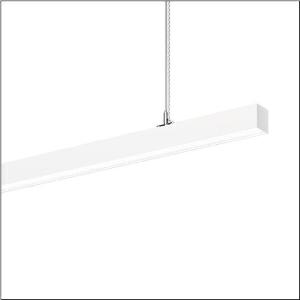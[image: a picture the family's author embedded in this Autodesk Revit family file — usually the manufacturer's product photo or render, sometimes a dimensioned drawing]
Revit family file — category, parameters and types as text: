
# Revit family: silica_21_51mx33dc4dwb
name_source: partatom
category: Lighting Fixtures
units: mm (PartAtom-declared; Revit-internal decimal feet)

## family parameters
Cut with Voids When Loaded = No
Host = Face
Light Source = No
Part Type = Normal
Room Calculation Point = No
Round Connector Dimension = Use Diameter
Shared = No

## types (1)
- --- (1 x LED, 14790 lm, 93.9 W, 4000K)
    Apparent Load = 94 VA
    CIE Flux Codes = 78 96 99 55 100
    Color Rendering = 80
    Color Temperature = 4000K
    Default Elevation = 1800 mm
    Description = Silica 21, office luminaire, primary optical cover: prismatic diffuser, of PMMA, CAT 2 (L<= 3000cd/m²), light emission: direct/indirect distribution, primary light characteristic: symmetric, installation type: suspended mounting, LED, rated luminous flux: 14.790lm, luminous efficacy: 158lm/W, light colour: 840, colour temperature: 4000K, control gear: DALI 2, with terminal, 3+2-pole, max. 2.5mm², mains connection: 220..240V, AC, 50/60Hz, rated input power: 93.9W, luminaire housing, of aluminium, traffic white (RAL 9016), length: 3.004mm, width: 53mm, height: 53mm, protection rating (complete): IP20, insulation class (complete): insulation class I (protective earthing), certification: CE, permissible operating ambient temperature: 0..+35°C, standard: EN 50419, packaging unit: 1 piece
    Height = 53 mm
    Lamp = 1 x LED
    Lamp Light Flux = 14790 lm
    Lamp Power = 93.9 W
    Lamp count = 1
    Length = 3004 mm
    Luminous efficacy = 158 lm/W
    Manufacturer = Siteco
    ModVariant = No
    Model = 51MX33DC4DWB
    Mounting Place = Ceiling
    Mounting Type = Pendant
    Number of Poles = 1
    OnlyDefault = Yes
    Power Factor = 1
    Product Name = Silica 21
    Product group = office luminaire | ceiling pendant
    ProductGroupID = 903
    Protection Class = Protection class I
    Protection Degree = IP 20
    RLX_Detail_Level = 1
    RLX_Emergency_Light_Flux = 0 lm
    RLX_Emergency_Type = 0
    RLX_Emergency_Type_DB = No
    RlxData = <blob elided: 21421 chars, md5=6268f690>
    Socket = socket
    Standby Power = 0 W
    System Light Flux = 14790 lm
    System Power = 94 W
    Type Comments = factory setting: luminous flux: 100 % | dim-lin: 254 | 323 mA
    Type Image = l_1349007.jpg
    URL = http://relux.com
    VarID = @adj_120559
    Voltage = 0 V
    Weight = 0.00 kg
    Width = 53 mm

## geometry (parser evidence)
native form markers: Blend x4, Sweep x11
no freeform markers — native parametric forms only
